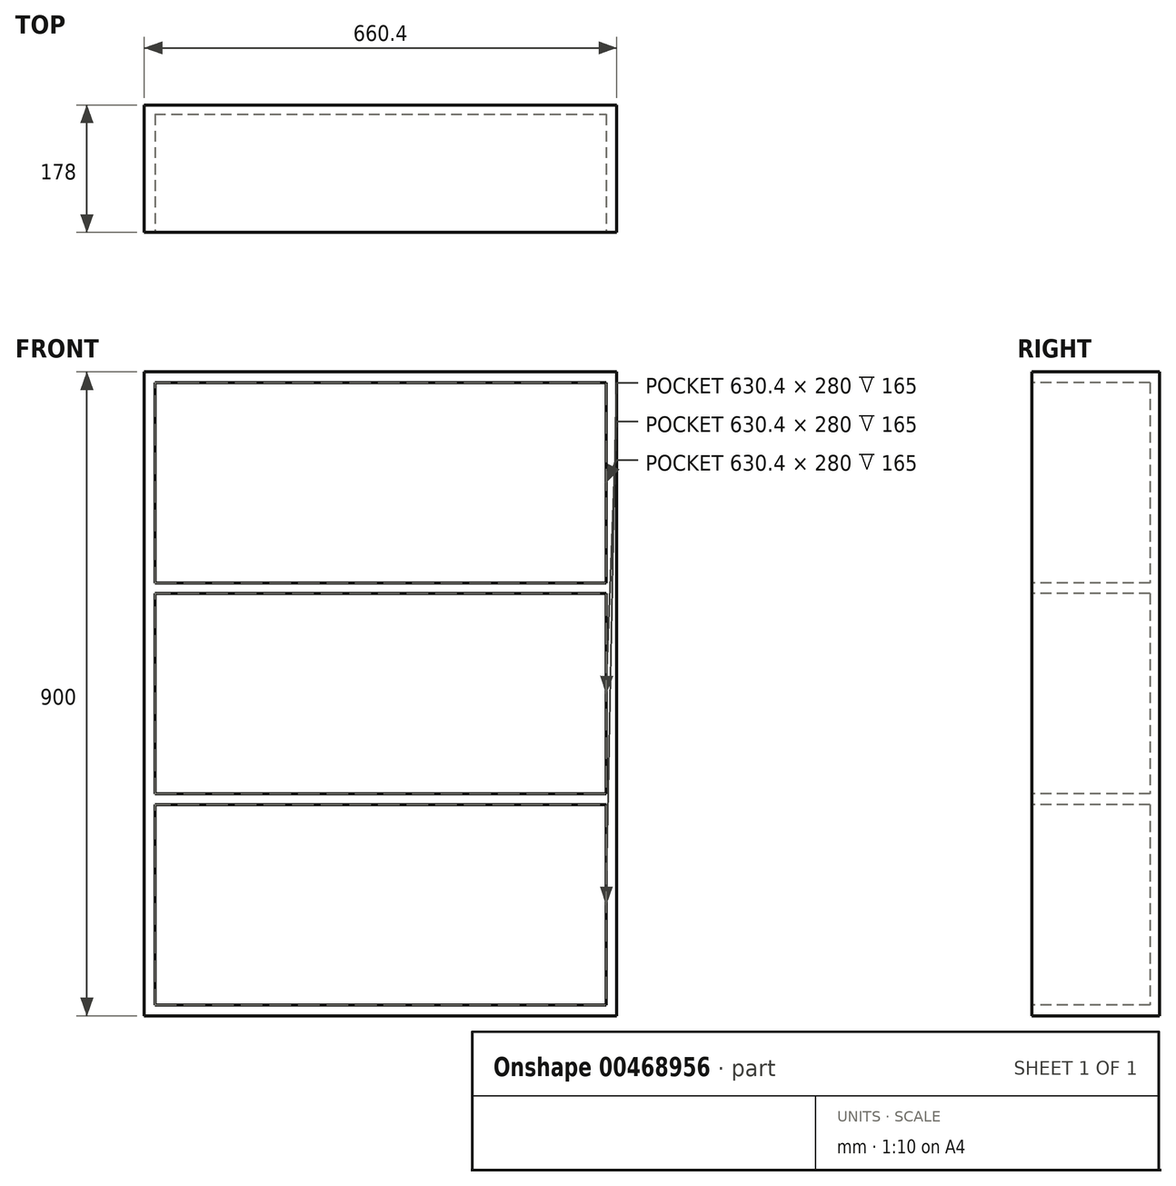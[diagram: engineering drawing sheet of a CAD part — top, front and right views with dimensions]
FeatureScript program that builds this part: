
annotation { "Feature Type Name" : "Feature", "Feature Type Description" : "" }
export const myFeature = defineFeature(function(context is Context, id is Id, definition is map)
    precondition{}
    {
        {
            var Q0;
            Q0=qCreatedBy(makeId("Top.planeOp"),FACE);
            var sketch = newSketch(context, id + "F0", { "sketchPlane" : qUnion([Q0])});
            skLineSegment(sketch, "E0.bottom", {"start": v(330.2, 89) * mm, "end": v(-330.2, 89) * mm});
            skLineSegment(sketch, "E0.top", {"start": v(330.2, -89) * mm, "end": v(-330.2, -89) * mm});
            skLineSegment(sketch, "E0.left", {"start": v(330.2, 89) * mm, "end": v(330.2, -89) * mm});
            skLineSegment(sketch, "E0.right", {"start": v(-330.2, 89) * mm, "end": v(-330.2, -89) * mm});
            skPoint(sketch, "E0.middle", {"position": v(0, 0) * mm});
            skSolve(sketch);
        }
        {
            var Q0;
            Q0 = qSketchRegion(id + "F0", true);
            extrude(context, id + "F1", {"entities" : qUnion([Q0]), "depth" : 900 * mm});
        }
        {
            var Q0;
            Q0=makeQuery(id+"F1.opExtrude","SWEPT_FACE",FACE,{"disambiguationData":[OSD([sQuery(id+"F0.wireOp",EDGE,"E0.top")])]});
            var sketch = newSketch(context, id + "F2", { "sketchPlane" : qUnion([Q0])});
            skLineSegment(sketch, "E1.bottom", {"start": v(-315.2, 885) * mm, "end": v(315.2, 885) * mm});
            skLineSegment(sketch, "E1.top", {"start": v(-315.2, 605) * mm, "end": v(315.2, 605) * mm});
            skLineSegment(sketch, "E1.left", {"start": v(-315.2, 885) * mm, "end": v(-315.2, 605) * mm});
            skLineSegment(sketch, "E1.right", {"start": v(315.2, 885) * mm, "end": v(315.2, 605) * mm});
            skLineSegment(sketch, "E2.bottom", {"start": v(-315.2, 590) * mm, "end": v(315.2, 590) * mm});
            skLineSegment(sketch, "E2.top", {"start": v(-315.2, 310) * mm, "end": v(315.2, 310) * mm});
            skLineSegment(sketch, "E2.left", {"start": v(-315.2, 590) * mm, "end": v(-315.2, 310) * mm});
            skLineSegment(sketch, "E2.right", {"start": v(315.2, 590) * mm, "end": v(315.2, 310) * mm});
            skLineSegment(sketch, "E3.bottom", {"start": v(-315.2, 295) * mm, "end": v(315.2, 295) * mm});
            skLineSegment(sketch, "E3.top", {"start": v(-315.2, 15) * mm, "end": v(315.2, 15) * mm});
            skLineSegment(sketch, "E3.left", {"start": v(-315.2, 295) * mm, "end": v(-315.2, 15) * mm});
            skLineSegment(sketch, "E3.right", {"start": v(315.2, 295) * mm, "end": v(315.2, 15) * mm});
            skSolve(sketch);
        }
        {
            var Q0;
            Q0=makeQuery(id+"F2.imprint","IMPRINT",FACE,{"disambiguationData":[TD([[makeQuery(id+"F2.imprint","IMPRINT",EDGE,{"derivedFrom":sQuery(id+"F2.wireOp",EDGE,"E1.bottom")}),-1.0]])]});
            var Q1;
            Q1=makeQuery(id+"F2.imprint","IMPRINT",FACE,{"disambiguationData":[TD([[makeQuery(id+"F2.imprint","IMPRINT",EDGE,{"derivedFrom":sQuery(id+"F2.wireOp",EDGE,"E2.bottom")}),-1.0]])]});
            var Q2;
            Q2=makeQuery(id+"F2.imprint","IMPRINT",FACE,{"disambiguationData":[TD([[makeQuery(id+"F2.imprint","IMPRINT",EDGE,{"derivedFrom":sQuery(id+"F2.wireOp",EDGE,"E3.bottom")}),-1.0]])]});
            extrude(context, id + "F3", {"entities" : qUnion([Q0, Q1, Q2]), "operationType" : NewBodyOperationType.REMOVE, "oppositeDirection" : true, "depth" : 165 * mm});
        }
    });
